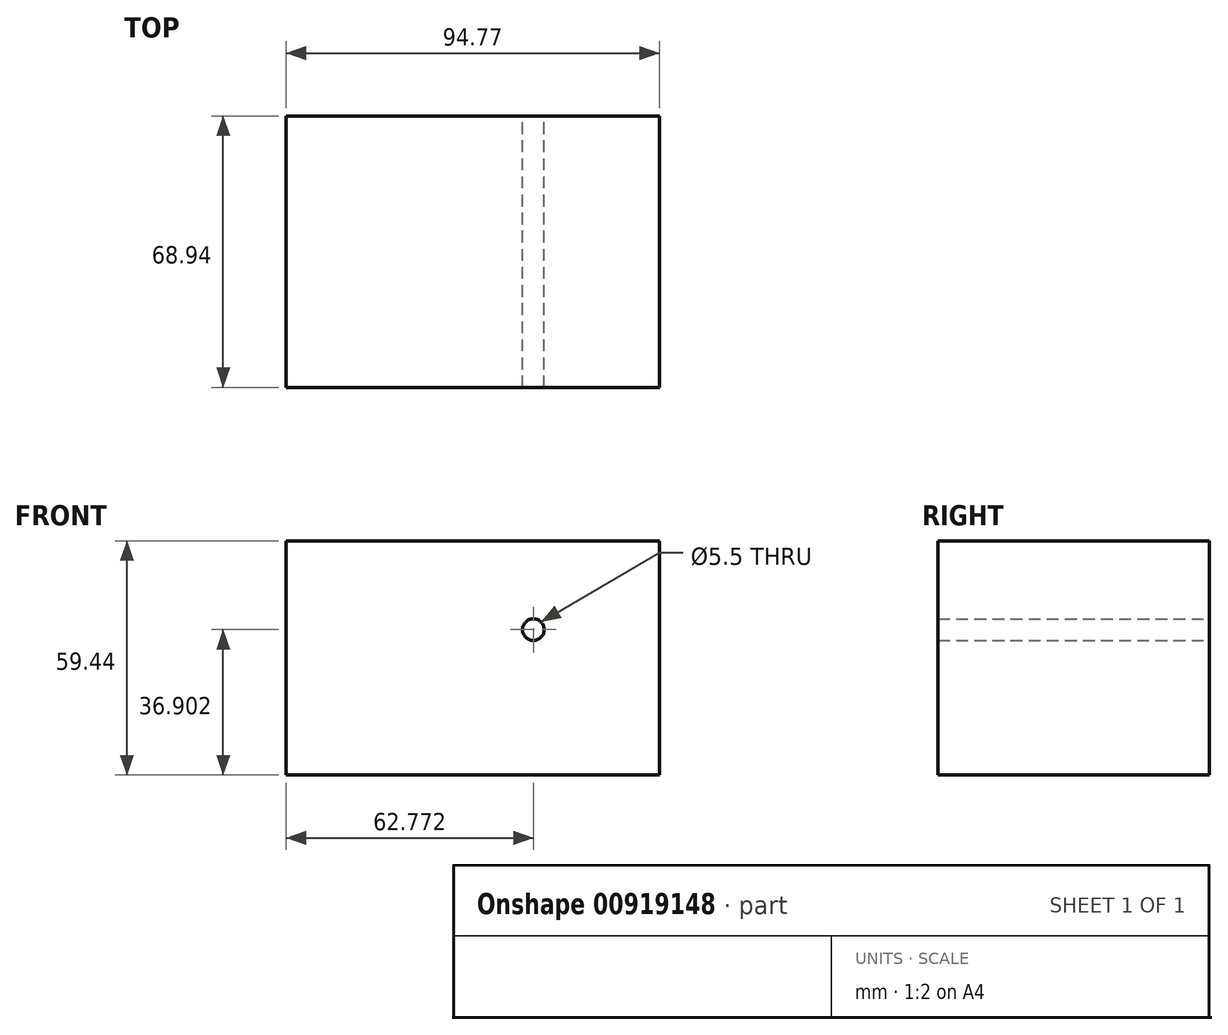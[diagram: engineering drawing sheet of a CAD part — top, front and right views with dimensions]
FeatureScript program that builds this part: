
annotation { "Feature Type Name" : "Feature", "Feature Type Description" : "" }
export const myFeature = defineFeature(function(context is Context, id is Id, definition is map)
    precondition{}
    {
        {
            var Q0;
            Q0=qCreatedBy(makeId("Top.planeOp"),FACE);
            var sketch = newSketch(context, id + "F0", { "sketchPlane" : qUnion([Q0])});
            skLineSegment(sketch, "E0.bottom", {"start": v(-52.69, 34.7) * mm, "end": v(42.08, 34.7) * mm});
            skLineSegment(sketch, "E0.top", {"start": v(-52.69, -34.24) * mm, "end": v(42.08, -34.24) * mm});
            skLineSegment(sketch, "E0.left", {"start": v(-52.69, 34.7) * mm, "end": v(-52.69, -34.24) * mm});
            skLineSegment(sketch, "E0.right", {"start": v(42.08, 34.7) * mm, "end": v(42.08, -34.24) * mm});
            skSolve(sketch);
        }
        {
            var Q0;
            Q0=makeQuery(id+"F0.imprint","IMPRINT",FACE,{"disambiguationData":[TD([[makeQuery(id+"F0.imprint","IMPRINT",EDGE,{"derivedFrom":sQuery(id+"F0.wireOp",EDGE,"E0.bottom")}),-1.0]])]});
            extrude(context, id + "F1", {"entities" : qUnion([Q0]), "depth" : 59.44 * mm, "offsetDistance" : 25.4 * mm});
        }
        {
            var Q0;
            Q0=makeQuery(id+"F1.opExtrude","SWEPT_FACE",FACE,{"disambiguationData":[OSD([sQuery(id+"F0.wireOp",EDGE,"E0.bottom")])]});
            var sketch = newSketch(context, id + "F2", { "sketchPlane" : qUnion([Q0])});
            skCircle(sketch, "E1", {"center": v(-10.08, 36.9) * mm, "radius": 14.41 * mm});
            skSolve(sketch);
        }
        {
            var Q0;
            Q0=sQuery(id+"F2.wireOp",VERTEX,"E1.center");
            var Q1;
            Q1=makeQuery(id+"F1.opExtrude","SWEPT_BODY",BODY,{"disambiguationData":[OSD([sQuery(id+"F0.wireOp",EDGE,"E0.bottom"),sQuery(id+"F0.wireOp",EDGE,"E0.top"),sQuery(id+"F0.wireOp",EDGE,"E0.left"),sQuery(id+"F0.wireOp",EDGE,"E0.right")])]});
            hole(context, id + "F3", {"style" : HoleStyle.SIMPLE, "endStyle" : HoleEndStyle.THROUGH, "standardTappedOrClearance" : lookupTablePath({ "fit" : "Normal", "standard" : "ISO", "size" : "M5", "type" : "Clearance" }), "standardBlindInLast" : lookupTablePath({ "fit" : "Normal", "standard" : "ISO", "size" : "M5", "type" : "Clearance" }), "holeDiameter" : 5.5 * mm, "majorDiameter" : 6.35 * mm, "isTappedThrough" : true, "tappedDepth" : 12.7 * mm, "tapClearance" : 3, "locations" : qUnion([Q0]), "scope" : qUnion([Q1])});
        }
    });
